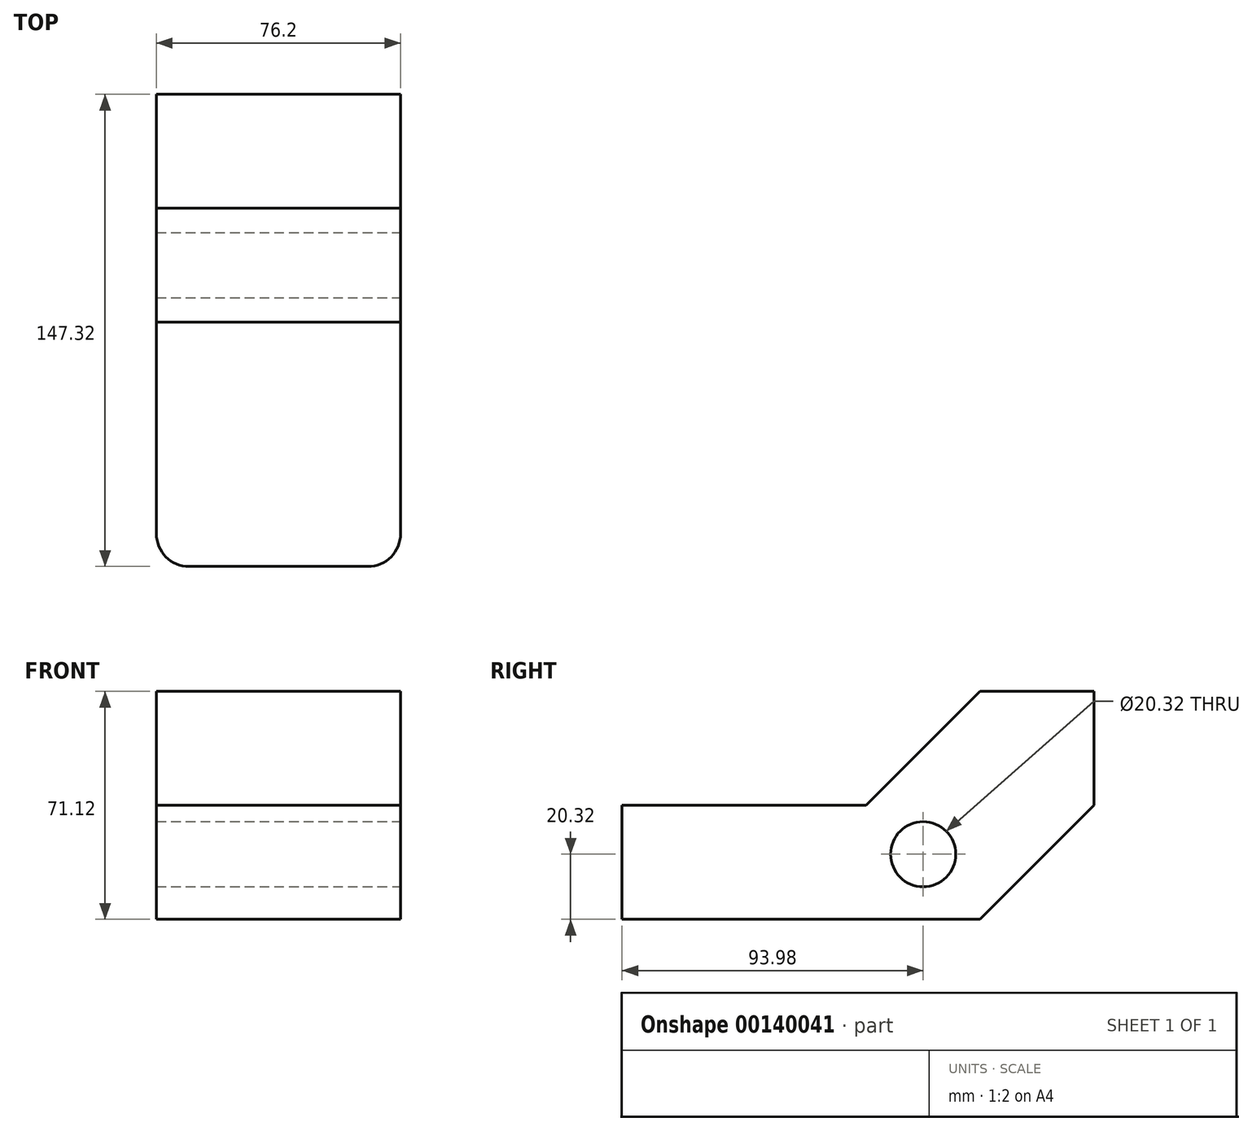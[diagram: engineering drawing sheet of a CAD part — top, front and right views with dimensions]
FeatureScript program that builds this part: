
annotation { "Feature Type Name" : "Feature", "Feature Type Description" : "" }
export const myFeature = defineFeature(function(context is Context, id is Id, definition is map)
    precondition{}
    {
        {
            var Q0;
            Q0=qCreatedBy(makeId("Right.planeOp"),FACE);
            var sketch = newSketch(context, id + "F0", { "sketchPlane" : qUnion([Q0])});
            skLineSegment(sketch, "E0", {"start": v(111.76, 0) * mm, "end": v(147.32, 35.56) * mm});
            skLineSegment(sketch, "E1", {"start": v(147.32, 35.56) * mm, "end": v(147.32, 71.12) * mm});
            skLineSegment(sketch, "E2", {"start": v(147.32, 71.12) * mm, "end": v(111.76, 71.12) * mm});
            skLineSegment(sketch, "E3", {"start": v(111.76, 71.12) * mm, "end": v(76.2, 35.56) * mm});
            skCircle(sketch, "E4", {"center": v(93.98, 20.32) * mm, "radius": 10.16 * mm});
            skLineSegment(sketch, "E5", {"start": v(76.2, 35.56) * mm, "end": v(76.2, 0) * mm});
            skLineSegment(sketch, "E6", {"start": v(76.2, 0) * mm, "end": v(111.76, 0) * mm});
            skLineSegment(sketch, "E7", {"start": v(0, 97.91) * mm, "end": v(0, -99.2) * mm, "construction": true});
            skLineSegment(sketch, "E8", {"start": v(-78.87, 0) * mm, "end": v(208.08, 0) * mm, "construction": true});
            skSolve(sketch);
        }
        {
            var Q0;
            Q0=qCreatedBy(makeId("Top.planeOp"),FACE);
            var sketch = newSketch(context, id + "F1", { "sketchPlane" : qUnion([Q0])});
            skLineSegment(sketch, "E9.bottom", {"start": v(-76.2, 76.2) * mm, "end": v(0, 76.2) * mm});
            skLineSegment(sketch, "E9.top", {"start": v(-66.04, 0) * mm, "end": v(-10.16, 0) * mm});
            skLineSegment(sketch, "E9.left", {"start": v(-76.2, 76.2) * mm, "end": v(-76.2, 10.16) * mm});
            skLineSegment(sketch, "E9.right", {"start": v(0, 76.2) * mm, "end": v(0, 10.16) * mm});
            skPoint(sketch, "E10.visualSharp", {"position": v(-76.2, 0) * mm});
            skArc(sketch, "E10.filletArc", {"start": v(-76.2, 10.16) * mm, "mid": v(-73.22, 2.98) * mm, "end": v(-66.04, 0) * mm});
            skPoint(sketch, "E11.visualSharp", {"position": v(0, 0) * mm});
            skArc(sketch, "E11.filletArc", {"start": v(-10.16, 0) * mm, "mid": v(-2.98, 2.98) * mm, "end": v(0, 10.16) * mm});
            skSolve(sketch);
        }
        {
            var Q0;
            Q0=makeQuery(id+"F1.imprint","IMPRINT",FACE,{"disambiguationData":[TD([[makeQuery(id+"F1.imprint","IMPRINT",EDGE,{"derivedFrom":sQuery(id+"F1.wireOp",EDGE,"E9.bottom")}),-1.0]])]});
            extrude(context, id + "F2", {"entities" : qUnion([Q0]), "depth" : 35.56 * mm});
        }
        {
            var Q0;
            Q0=makeQuery(id+"F0.imprint","IMPRINT",FACE,{"disambiguationData":[TD([[makeQuery(id+"F0.imprint","IMPRINT",EDGE,{"derivedFrom":sQuery(id+"F0.wireOp",EDGE,"V167pyjI-80nj-bJ5f-TowH-XsFyjwHX5xVf")}),1.0]])]});
            var Q1;
            Q1=makeQuery(id+"F0.imprint","IMPRINT",FACE,{"disambiguationData":[TD([[makeQuery(id+"F0.imprint","IMPRINT",EDGE,{"derivedFrom":sQuery(id+"F0.wireOp",EDGE,"E0")}),1.0]])]});
            extrude(context, id + "F3", {"entities" : qUnion([Q0, Q1]), "operationType" : NewBodyOperationType.ADD, "oppositeDirection" : true, "depth" : 76.2 * mm});
        }
    });
